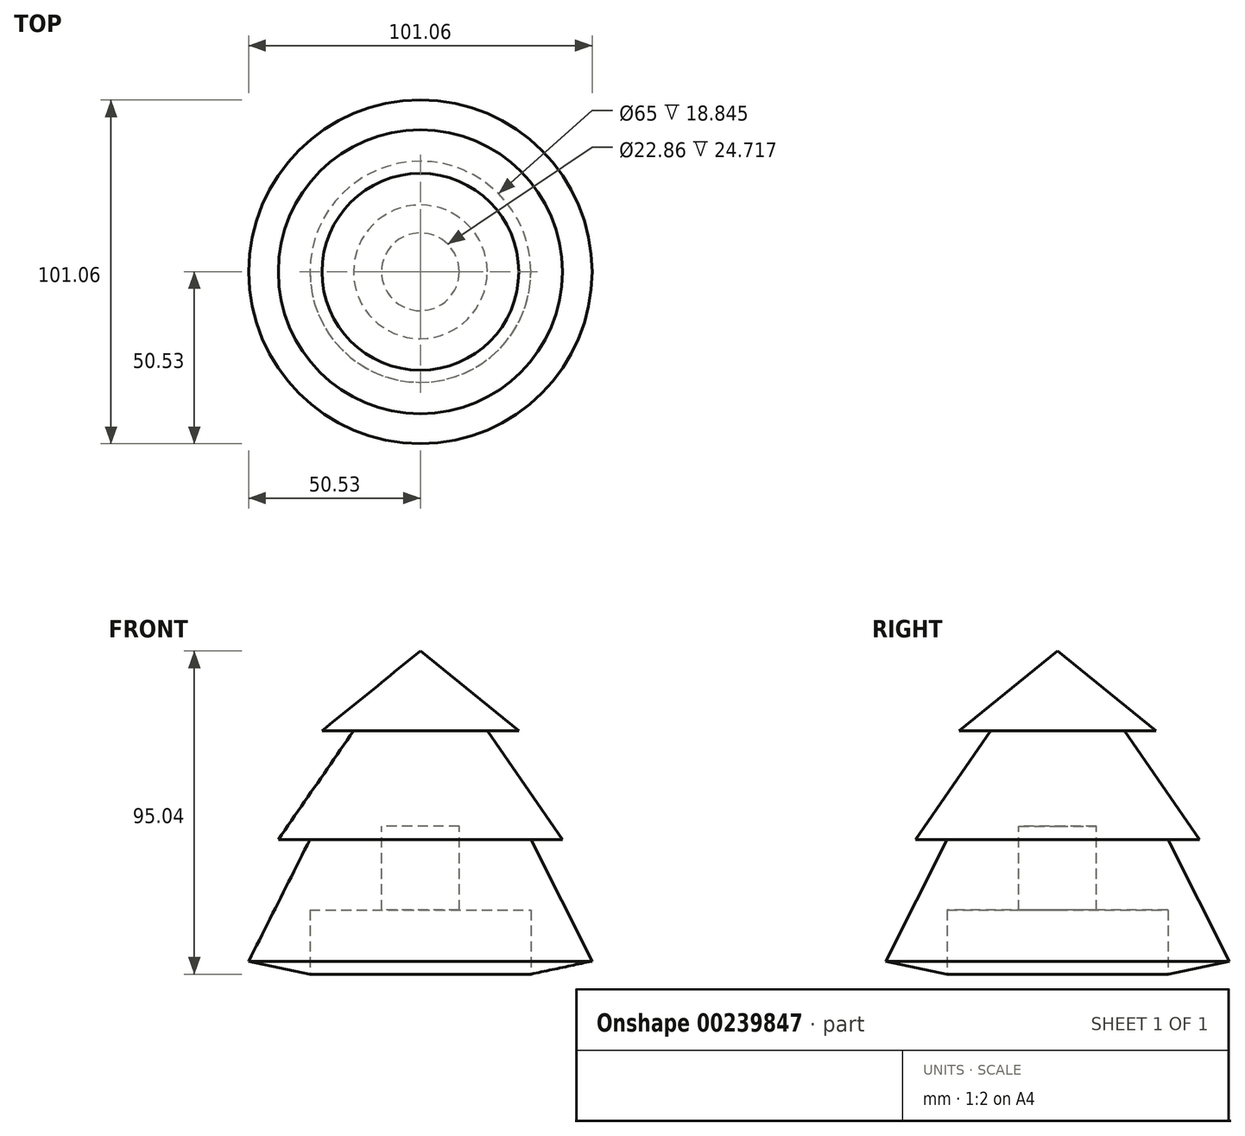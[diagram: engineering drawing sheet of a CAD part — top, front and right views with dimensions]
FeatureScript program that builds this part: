
annotation { "Feature Type Name" : "Feature", "Feature Type Description" : "" }
export const myFeature = defineFeature(function(context is Context, id is Id, definition is map)
    precondition{}
    {
        {
            var Q0;
            Q0=qCreatedBy(makeId("Front.planeOp"),FACE);
            var sketch = newSketch(context, id + "F0", { "sketchPlane" : qUnion([Q0])});
            skLineSegment(sketch, "E0", {"start": v(0, 51.48) * mm, "end": v(-28.95, 28) * mm});
            skLineSegment(sketch, "E1", {"start": v(-28.95, 28) * mm, "end": v(-19.66, 28) * mm});
            skLineSegment(sketch, "E2", {"start": v(-19.66, 28) * mm, "end": v(-41.79, -3.96) * mm});
            skLineSegment(sketch, "E3", {"start": v(-41.79, -3.96) * mm, "end": v(-32.5, -3.96) * mm});
            skLineSegment(sketch, "E4", {"start": v(-32.5, -3.96) * mm, "end": v(-50.53, -39.74) * mm});
            skLineSegment(sketch, "E5", {"start": v(-50.53, -39.74) * mm, "end": v(-32.5, -43.56) * mm});
            skLineSegment(sketch, "E6", {"start": v(-32.5, -43.56) * mm, "end": v(-32.5, -50.12) * mm});
            skLineSegment(sketch, "E7", {"start": v(-32.5, -50.12) * mm, "end": v(0, -50.12) * mm});
            skLineSegment(sketch, "E8", {"start": v(0, -50.12) * mm, "end": v(0, 51.48) * mm});
            skSolve(sketch);
        }
        {
            var Q0;
            Q0 = qSketchRegion(id + "F0", true);
            var Q1;
            Q1=sQuery(id+"F0.wireOp",EDGE,"E8");
            revolve(context, id + "F1", {"entities" : qUnion([Q0]), "axis" : qUnion([Q1]), "revolveType" : RevolveType.FULL});
        }
        {
            var Q0;
            Q0=makeQuery(id+"F1.opRevolve","SWEPT_FACE",FACE,{"disambiguationData":[OSD([sQuery(id+"F0.wireOp",EDGE,"E7")])]});
            extrude(context, id + "F2", {"entities" : qUnion([Q0]), "operationType" : NewBodyOperationType.REMOVE, "oppositeDirection" : true, "depth" : 25.4 * mm});
        }
        {
            var Q0;
            Q0=qCreatedBy(makeId("Top.planeOp"),FACE);
            var sketch = newSketch(context, id + "F3", { "sketchPlane" : qUnion([Q0])});
            skCircle(sketch, "E9", {"center": v(0, 0) * mm, "radius": 11.43 * mm});
            skSolve(sketch);
        }
        {
            var Q0;
            Q0 = qSketchRegion(id + "F3", true);
            extrude(context, id + "F4", {"entities" : qUnion([Q0]), "operationType" : NewBodyOperationType.REMOVE, "oppositeDirection" : true, "depth" : 84.33 * mm});
        }
    });
